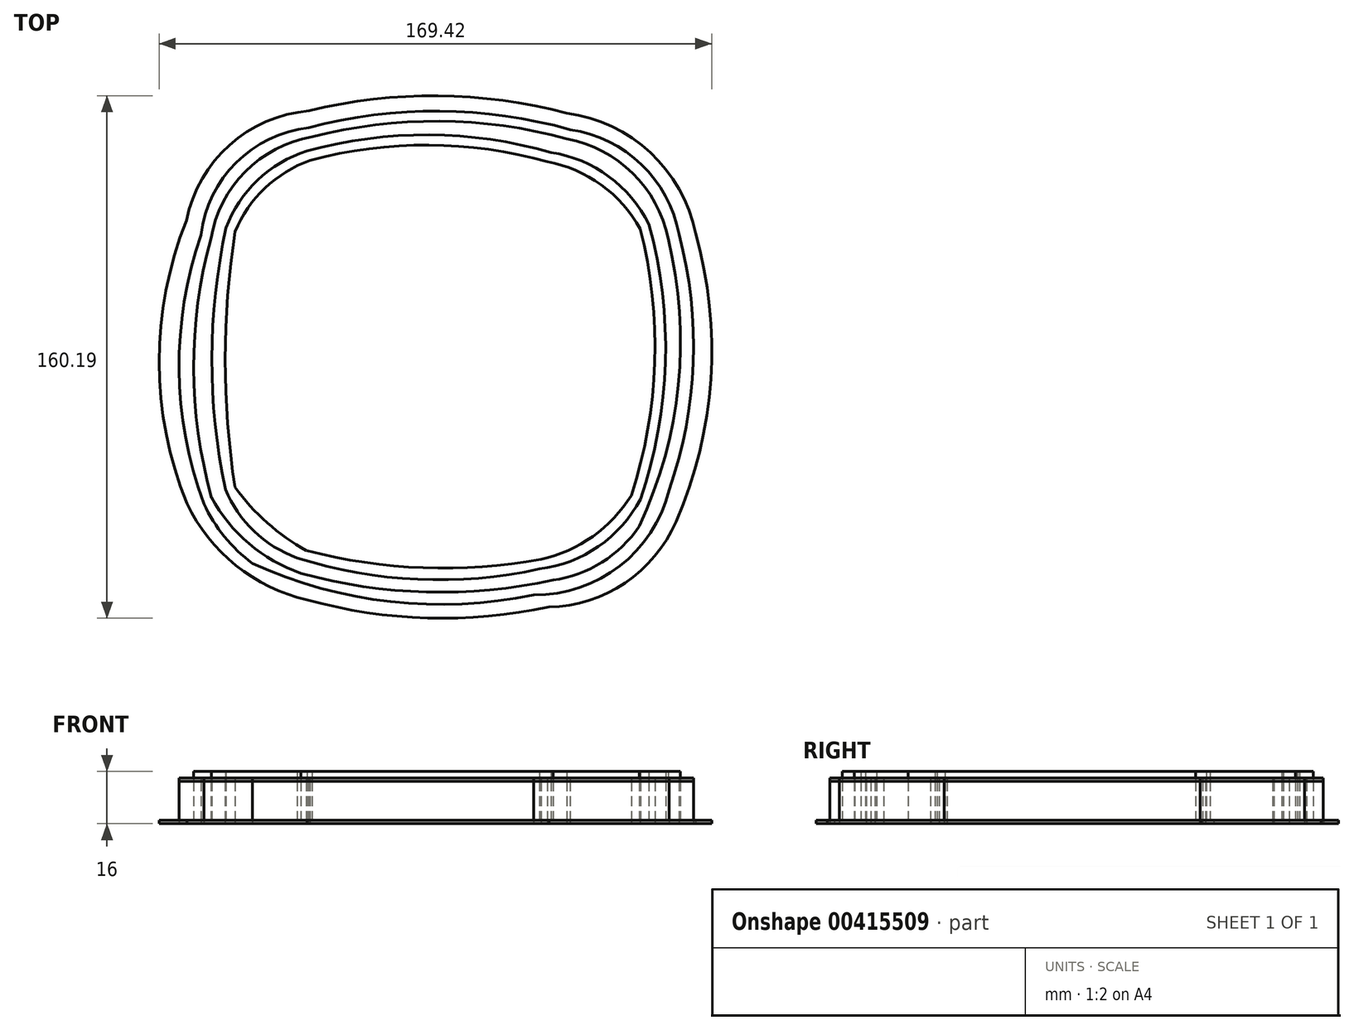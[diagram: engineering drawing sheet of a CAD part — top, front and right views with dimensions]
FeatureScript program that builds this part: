
annotation { "Feature Type Name" : "Feature", "Feature Type Description" : "" }
export const myFeature = defineFeature(function(context is Context, id is Id, definition is map)
    precondition{}
    {
        {
            var Q0;
            Q0=qCreatedBy(makeId("Top.planeOp"),FACE);
            var sketch = newSketch(context, id + "F0", { "sketchPlane" : qUnion([Q0])});
            skArc(sketch, "E0", {"start": v(36.68, 59.11) * mm, "mid": v(-2.33, 64.52) * mm, "end": v(-41.41, 59.67) * mm});
            skArc(sketch, "E1", {"start": v(67.8, 28.48) * mm, "mid": v(56.9, 48.54) * mm, "end": v(36.68, 59.11) * mm});
            skArc(sketch, "E2", {"start": v(58.94, -59.65) * mm, "mid": v(70.89, -16.34) * mm, "end": v(67.8, 28.48) * mm});
            skArc(sketch, "E3", {"start": v(32.46, -76.21) * mm, "mid": v(47.47, -70.77) * mm, "end": v(58.94, -59.65) * mm});
            skArc(sketch, "E4", {"start": v(-44.84, -74.12) * mm, "mid": v(-6.32, -79.84) * mm, "end": v(32.46, -76.21) * mm});
            skArc(sketch, "E5", {"start": v(-41.41, 59.67) * mm, "mid": v(-61.9, 49.03) * mm, "end": v(-72.41, 28.48) * mm});
            skArc(sketch, "E6", {"start": v(31.86, 54.91) * mm, "mid": v(-5.51, 60.32) * mm, "end": v(-42.95, 55.36) * mm});
            skArc(sketch, "E7", {"start": v(61.9, 32.88) * mm, "mid": v(49.59, 47.58) * mm, "end": v(31.86, 54.91) * mm});
            skArc(sketch, "E8", {"start": v(-42.95, 55.36) * mm, "mid": v(-58.1, 46.45) * mm, "end": v(-67.76, 31.77) * mm});
            skArc(sketch, "E9", {"start": v(-67.76, 31.77) * mm, "mid": v(-72.1, -8.26) * mm, "end": v(-68, -48.3) * mm});
            skArc(sketch, "E10", {"start": v(-68, -48.3) * mm, "mid": v(-59.2, -61.19) * mm, "end": v(-45.93, -69.37) * mm});
            skArc(sketch, "E11", {"start": v(-45.93, -69.37) * mm, "mid": v(-9.03, -75.96) * mm, "end": v(28.32, -72.8) * mm});
            skArc(sketch, "E12", {"start": v(28.32, -72.8) * mm, "mid": v(46.43, -65.88) * mm, "end": v(59.28, -51.37) * mm});
            skArc(sketch, "E13", {"start": v(59.28, -51.37) * mm, "mid": v(66.94, -9.44) * mm, "end": v(61.9, 32.88) * mm});
            skLineSegment(sketch, "E14", {"start": v(36.67, 59.11) * mm, "end": v(36.67, 59.12) * mm});
            skArc(sketch, "E15", {"start": v(37.76, 61.9) * mm, "mid": v(-2.26, 67.64) * mm, "end": v(-42.36, 62.52) * mm});
            skArc(sketch, "E16", {"start": v(30.74, 52.13) * mm, "mid": v(-5.6, 57.17) * mm, "end": v(-42, 52.51) * mm});
            skArc(sketch, "E17", {"start": v(71.13, 29.84) * mm, "mid": v(59.6, 51.24) * mm, "end": v(37.76, 61.9) * mm});
            skArc(sketch, "E18", {"start": v(59.24, 31.5) * mm, "mid": v(47.27, 44.97) * mm, "end": v(30.74, 52.13) * mm});
            skArc(sketch, "E19", {"start": v(-42.36, 62.52) * mm, "mid": v(-64.64, 51.84) * mm, "end": v(-75.47, 29.63) * mm});
            skArc(sketch, "E20", {"start": v(-42, 52.51) * mm, "mid": v(-55.82, 44) * mm, "end": v(-65, 30.61) * mm});
            skArc(sketch, "E21", {"start": v(-72.21, -50.83) * mm, "mid": v(-60.7, -65.04) * mm, "end": v(-44.84, -74.12) * mm});
            skArc(sketch, "E22", {"start": v(-72.41, 28.48) * mm, "mid": v(-77.7, -11.2) * mm, "end": v(-72.21, -50.83) * mm});
            skArc(sketch, "E23", {"start": v(-75.47, 29.63) * mm, "mid": v(-82.15, -11.65) * mm, "end": v(-74.57, -52.77) * mm});
            skArc(sketch, "E24", {"start": v(-74.57, -52.77) * mm, "mid": v(-68.27, -62.86) * mm, "end": v(-59.68, -71.1) * mm});
            skArc(sketch, "E25", {"start": v(-59.68, -71.1) * mm, "mid": v(-17.32, -82.8) * mm, "end": v(26.57, -80.75) * mm});
            skArc(sketch, "E26", {"start": v(68.1, -48.58) * mm, "mid": v(75.48, -9.6) * mm, "end": v(71.13, 29.84) * mm});
            skArc(sketch, "E27", {"start": v(56.51, -50.2) * mm, "mid": v(63.66, -9.55) * mm, "end": v(59.24, 31.5) * mm});
            skArc(sketch, "E28", {"start": v(-65, 30.61) * mm, "mid": v(-68.01, -8.55) * mm, "end": v(-65.02, -47.7) * mm});
            skArc(sketch, "E29", {"start": v(-65.02, -47.7) * mm, "mid": v(-55.15, -58.64) * mm, "end": v(-43.1, -67.12) * mm});
            skArc(sketch, "E30", {"start": v(-43.1, -67.12) * mm, "mid": v(-7.3, -72.4) * mm, "end": v(28.8, -69.79) * mm});
            skArc(sketch, "E31", {"start": v(28.8, -69.79) * mm, "mid": v(44.66, -62.83) * mm, "end": v(56.51, -50.2) * mm});
            skArc(sketch, "E32", {"start": v(-42.94, -82.25) * mm, "mid": v(-5.98, -87.83) * mm, "end": v(31.25, -84.45) * mm});
            skArc(sketch, "E33", {"start": v(-79.78, -52.72) * mm, "mid": v(-64.73, -71.68) * mm, "end": v(-42.94, -82.25) * mm});
            skArc(sketch, "E34", {"start": v(-79.89, 34.06) * mm, "mid": v(-88.28, -9.34) * mm, "end": v(-79.78, -52.72) * mm});
            skArc(sketch, "E35", {"start": v(-42.28, 67.7) * mm, "mid": v(-66.72, 57.18) * mm, "end": v(-79.89, 34.06) * mm});
            skArc(sketch, "E36", {"start": v(36.68, 66.98) * mm, "mid": v(-2.75, 72.3) * mm, "end": v(-42.28, 67.7) * mm});
            skArc(sketch, "E37", {"start": v(76.14, 30.13) * mm, "mid": v(62.32, 54.88) * mm, "end": v(36.68, 66.98) * mm});
            skArc(sketch, "E38", {"start": v(70.2, -58.21) * mm, "mid": v(80.85, -14.56) * mm, "end": v(76.14, 30.13) * mm});
            skArc(sketch, "E39", {"start": v(31.25, -84.45) * mm, "mid": v(54.58, -77.05) * mm, "end": v(70.2, -58.21) * mm});
            skArc(sketch, "E40", {"start": v(26.57, -80.75) * mm, "mid": v(52.93, -71.89) * mm, "end": v(68.1, -48.58) * mm});
            skSolve(sketch);
        }
        {
            var Q0;
            Q0=makeQuery(id+"F0.imprint","IMPRINT",FACE,{"disambiguationData":[TD([[makeQuery(id+"F0.imprint","IMPRINT",EDGE,{"derivedFrom":sQuery(id+"F0.wireOp",EDGE,"E16")}),1.0]])]});
            var Q1;
            Q1=makeQuery(id+"F0.imprint","IMPRINT",FACE,{"disambiguationData":[TD([[makeQuery(id+"F0.imprint","IMPRINT",EDGE,{"derivedFrom":sQuery(id+"F0.wireOp",EDGE,"E15")}),-1.0]])]});
            extrude(context, id + "F1", {"entities" : qUnion([Q0, Q1]), "depth" : 1 * mm});
        }
        {
            var Q0;
            {var subQ1=sQuery(id+"F0.wireOp",EDGE,"E1");Q0=makeQuery(id+"F0.imprint","IMPRINT",FACE,{"disambiguationData":[TD([[makeQuery(id+"F0.imprint","IMPRINT",EDGE,{"derivedFrom":subQ1}),-1.0]])]});}
            var Q1;
            Q1=makeQuery(id+"F0.imprint","IMPRINT",FACE,{"disambiguationData":[TD([[makeQuery(id+"F0.imprint","IMPRINT",EDGE,{"derivedFrom":sQuery(id+"F0.wireOp",EDGE,"E6")}),1.0]])]});
            extrude(context, id + "F2", {"entities" : qUnion([Q0, Q1]), "depth" : 13 * mm});
        }
        {
            var Q0;
            Q0=makeQuery(id+"F2.opExtrude","CAP_FACE",FACE,{"disambiguationData":[OSD([sQuery(id+"F0.wireOp",EDGE,"E6"),sQuery(id+"F0.wireOp",EDGE,"E7"),sQuery(id+"F0.wireOp",EDGE,"E8"),sQuery(id+"F0.wireOp",EDGE,"E9"),sQuery(id+"F0.wireOp",EDGE,"E10"),sQuery(id+"F0.wireOp",EDGE,"E11"),sQuery(id+"F0.wireOp",EDGE,"E12"),sQuery(id+"F0.wireOp",EDGE,"E13"),sQuery(id+"F0.wireOp",EDGE,"E16"),sQuery(id+"F0.wireOp",EDGE,"E18"),sQuery(id+"F0.wireOp",EDGE,"E20"),sQuery(id+"F0.wireOp",EDGE,"E27"),sQuery(id+"F0.wireOp",EDGE,"E28"),sQuery(id+"F0.wireOp",EDGE,"E29"),sQuery(id+"F0.wireOp",EDGE,"E30"),sQuery(id+"F0.wireOp",EDGE,"E31")])],"isStart":false});
            cPlane(context, id + "F3", {"entities" : qUnion([Q0]), "cplaneType" : CPlaneType.OFFSET, "offset" : 0 * mm, "width" : 150 * mm, "height" : 150 * mm});
        }
        {
            var Q0;
            Q0=makeQuery(id+"F2.opExtrude","CAP_FACE",FACE,{"disambiguationData":[OSD([sQuery(id+"F0.wireOp",EDGE,"E0"),sQuery(id+"F0.wireOp",EDGE,"E1"),sQuery(id+"F0.wireOp",EDGE,"E2"),sQuery(id+"F0.wireOp",EDGE,"E3"),sQuery(id+"F0.wireOp",EDGE,"E4"),sQuery(id+"F0.wireOp",EDGE,"E5"),sQuery(id+"F0.wireOp",EDGE,"E15"),sQuery(id+"F0.wireOp",EDGE,"E17"),sQuery(id+"F0.wireOp",EDGE,"E19"),sQuery(id+"F0.wireOp",EDGE,"E21"),sQuery(id+"F0.wireOp",EDGE,"E22"),sQuery(id+"F0.wireOp",EDGE,"E23"),sQuery(id+"F0.wireOp",EDGE,"E24"),sQuery(id+"F0.wireOp",EDGE,"E25"),sQuery(id+"F0.wireOp",EDGE,"R3zJ5CH1-gCmS-84no-yaRp-lFJkKYCt01A0"),sQuery(id+"F0.wireOp",EDGE,"E26")])],"isStart":false});
            var Q1;
            Q1=makeQuery(id+"F2.opExtrude","CAP_FACE",FACE,{"disambiguationData":[OSD([sQuery(id+"F0.wireOp",EDGE,"E6"),sQuery(id+"F0.wireOp",EDGE,"E7"),sQuery(id+"F0.wireOp",EDGE,"E8"),sQuery(id+"F0.wireOp",EDGE,"E9"),sQuery(id+"F0.wireOp",EDGE,"E10"),sQuery(id+"F0.wireOp",EDGE,"E11"),sQuery(id+"F0.wireOp",EDGE,"E12"),sQuery(id+"F0.wireOp",EDGE,"E13"),sQuery(id+"F0.wireOp",EDGE,"E16"),sQuery(id+"F0.wireOp",EDGE,"E18"),sQuery(id+"F0.wireOp",EDGE,"E20"),sQuery(id+"F0.wireOp",EDGE,"E27"),sQuery(id+"F0.wireOp",EDGE,"E28"),sQuery(id+"F0.wireOp",EDGE,"E29"),sQuery(id+"F0.wireOp",EDGE,"E30"),sQuery(id+"F0.wireOp",EDGE,"E31")])],"isStart":false});
            extrude(context, id + "F4", {"entities" : qUnion([Q0, Q1]), "depth" : 1 * mm});
        }
        {
            var Q0;
            {var subQ1=sQuery(id+"F0.wireOp",EDGE,"E1");Q0=makeQuery(id+"F0.imprint","IMPRINT",FACE,{"disambiguationData":[TD([[makeQuery(id+"F0.imprint","IMPRINT",EDGE,{"derivedFrom":subQ1}),1.0]])]});}
            extrude(context, id + "F5", {"entities" : qUnion([Q0]), "depth" : 16 * mm});
        }
        {
            var Q0;
            Q0=makeQuery(id+"F5.opExtrude","CAP_FACE",FACE,{"disambiguationData":[OSD([sQuery(id+"F0.wireOp",EDGE,"E0"),sQuery(id+"F0.wireOp",EDGE,"E1"),sQuery(id+"F0.wireOp",EDGE,"E2"),sQuery(id+"F0.wireOp",EDGE,"E3"),sQuery(id+"F0.wireOp",EDGE,"E4"),sQuery(id+"F0.wireOp",EDGE,"E5"),sQuery(id+"F0.wireOp",EDGE,"E6"),sQuery(id+"F0.wireOp",EDGE,"E7"),sQuery(id+"F0.wireOp",EDGE,"E8"),sQuery(id+"F0.wireOp",EDGE,"E9"),sQuery(id+"F0.wireOp",EDGE,"E10"),sQuery(id+"F0.wireOp",EDGE,"E11"),sQuery(id+"F0.wireOp",EDGE,"E12"),sQuery(id+"F0.wireOp",EDGE,"E13"),sQuery(id+"F0.wireOp",EDGE,"E21"),sQuery(id+"F0.wireOp",EDGE,"E22")])],"isStart":true});
            extrude(context, id + "F6", {"entities" : qUnion([Q0]), "operationType" : NewBodyOperationType.REMOVE, "oppositeDirection" : true, "depth" : 14 * mm});
        }
    });
